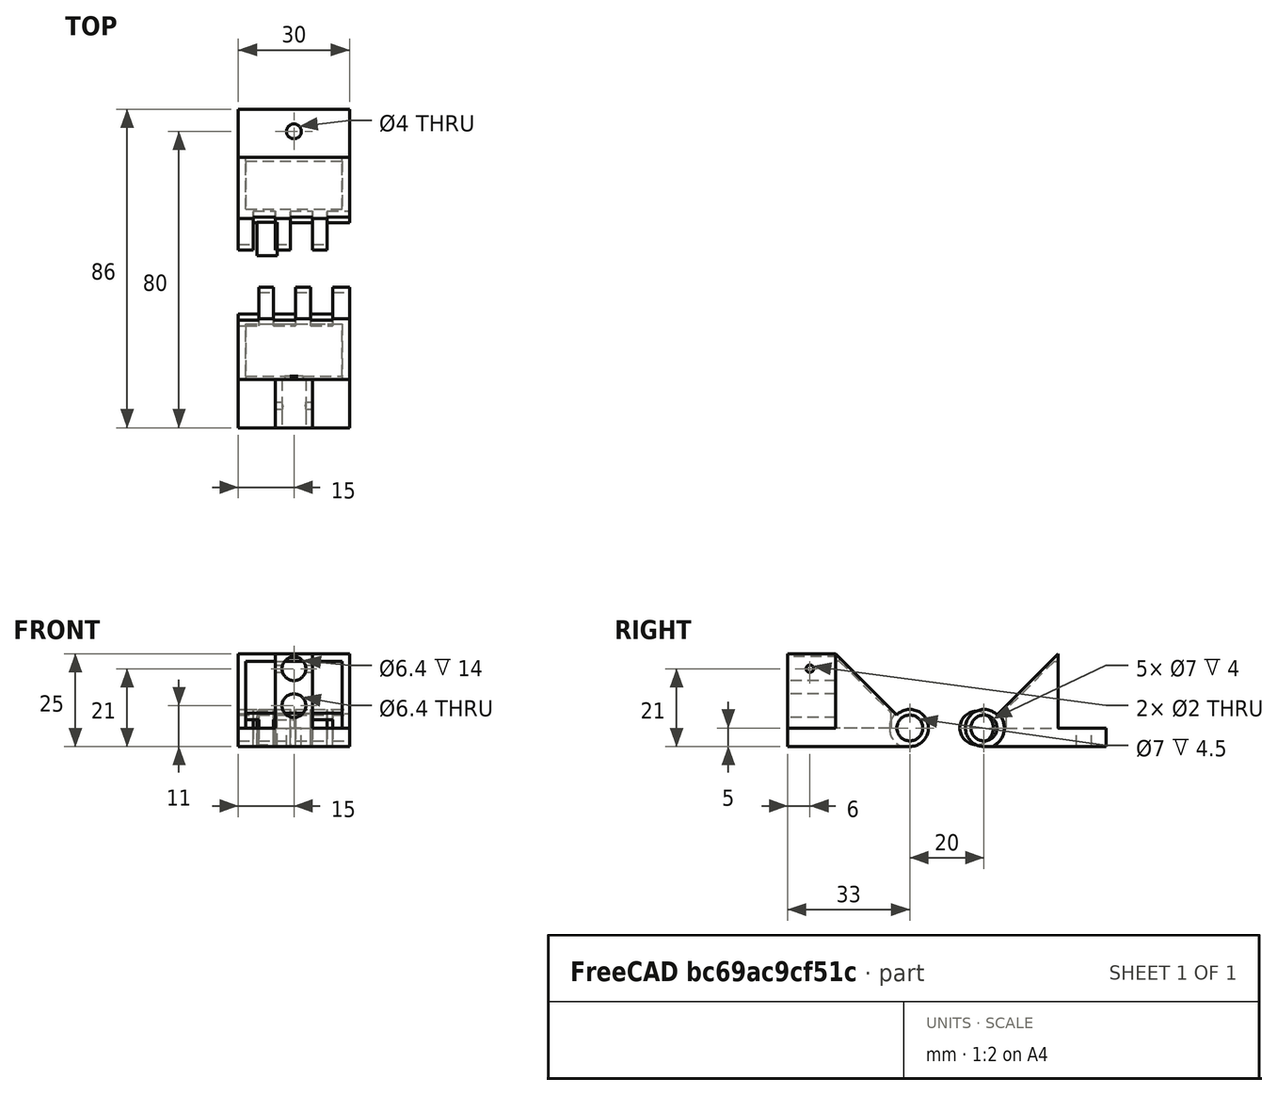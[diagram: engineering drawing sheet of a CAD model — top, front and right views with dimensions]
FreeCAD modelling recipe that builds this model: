
FCSTD DOCUMENT  (FreeCAD 0.16R6703 (Git))
Label: hinge_v3_0
License: CreativeCommons Attribution-ShareAlike
LicenseURL: http://creativecommons.org/licenses/by-sa/4.0/
objects: Part::Cut×12, Part::Box×11, Part::Cylinder×11, Part::MultiFuse×4, Part::FeaturePython×2, Part::Mirroring×1
note: 41 computed .brp shape members not serialized (recipe doc carries the construction recipe); baked Part::Feature solids carry a one-line shape summary decoded from their .brp

FEATURE [Part::Box] Box  label="Cube_out"
  Height = 20
  Length = 30
  Placement = pos=(-15,-5,-10) rot=(0,0,1;0rad)
  Width = 20
FEATURE [Part::Box] Box001  label="Cube_out_cut"
  Height = 15
  Length = 30
  Placement = pos=(-15,-5,-10) rot=(1,0,0;0.785398rad)
  Width = 34
FEATURE [Part::Cut] Cut
  Base = -> Box
  Tool = -> Box001
FEATURE [Part::Box] Box002  label="base"
  Height = 5
  Length = 30
  Placement = pos=(-15,-5,-15) rot=(0,0,1;0rad)
  Width = 33
FEATURE [Part::Cylinder] Cylinder  label="eje_out"
  Angle = 360
  Height = 30
  Placement = pos=(-15,-5,-10) rot=(0,1,0;1.5708rad)
  Radius = 5
FEATURE [Part::Box] Box003  label="Cube_int"
  Height = 18
  Length = 26
  Placement = pos=(-13,1,-10) rot=(0,0,1;0rad)
  Width = 20
FEATURE [Part::Box] Box004  label="Cube_int_cut"
  Height = 15
  Length = 30
  Placement = pos=(-15,-4,-10) rot=(1,0,0;0.785398rad)
  Width = 34
FEATURE [Part::Cut] Cut001
  Base = -> Box003
  Tool = -> Box004
FEATURE [Part::Cut] Cut002
  Base = -> Cut
  Tool = -> Cut001
FEATURE [Part::Cylinder] Cylinder001  label="eje_int"
  Angle = 360
  Height = 30
  Placement = pos=(-15,-5,-10) rot=(0,1,0;1.5708rad)
  Radius = 3.5
FEATURE [Part::MultiFuse] Fusion
  Shapes = -> [Cut002,Box002,Cylinder]
FEATURE [Part::Cut] Cut003
  Base = -> Fusion
  Tool = -> Cylinder001
FEATURE [Part::Box] Box005  label="Cube_out001"
  Height = 20
  Length = 30
  Placement = pos=(-15,-5,-10) rot=(0,0,1;0rad)
  Width = 20
FEATURE [Part::Box] Box006  label="Cube_out_cut001"
  Height = 15
  Length = 30
  Placement = pos=(-15,-5,-10) rot=(1,0,0;0.785398rad)
  Width = 34
FEATURE [Part::Cut] Cut004
  Base = -> Box005
  Tool = -> Box006
FEATURE [Part::Box] Box007  label="base001"
  Height = 5
  Length = 30
  Placement = pos=(-15,-5,-15) rot=(0,0,1;0rad)
  Width = 33
FEATURE [Part::Cylinder] Cylinder002  label="eje_out001"
  Angle = 360
  Height = 30
  Placement = pos=(-15,-5,-10) rot=(0,1,0;1.5708rad)
  Radius = 5
FEATURE [Part::Box] Box008  label="Cube_int001"
  Height = 18
  Length = 26
  Placement = pos=(-13,0,-10) rot=(0,0,1;0rad)
  Width = 20
FEATURE [Part::Box] Box009  label="Cube_int_cut001"
  Height = 15
  Length = 30
  Placement = pos=(-15,-4,-10) rot=(1,0,0;0.785398rad)
  Width = 34
FEATURE [Part::Cut] Cut005
  Base = -> Box008
  Tool = -> Box009
FEATURE [Part::Cut] Cut006
  Base = -> Cut004
  Tool = -> Cut005
FEATURE [Part::Cylinder] Cylinder003  label="eje_int001"
  Angle = 360
  Height = 30
  Placement = pos=(-15,-5,-10) rot=(0,1,0;1.5708rad)
  Radius = 3.5
FEATURE [Part::MultiFuse] Fusion001
  Shapes = -> [Cut006,Box007,Cylinder002]
FEATURE [Part::Cut] Cut007
  Base = -> Fusion001
  Tool = -> Cylinder003
FEATURE [Part::Mirroring] Part__Mirroring  label="Cut007 (Mirror #1)"
  Base = (0,-15,0)
  Normal = (0,1,0)
  Source = -> Cut007
FEATURE [Part::Cylinder] Cylinder004  label="eje_out002"
  Angle = 360
  Height = 6
  Placement = pos=(-11,-5,-10) rot=(0,1,0;1.5708rad)
  Radius = 5.5
FEATURE [Part::FeaturePython] Array  # Draft array (typed FeaturePython)
  Angle = 360
  ArrayType = 0
  Axis = (1,0,0)
  Base = -> Cylinder004
  Center = (0,0,0)
  Fuse = false
  IntervalAxis = (0,0,0)
  IntervalX = (10,0,0)
  IntervalY = (0,0,0)
  IntervalZ = (0,0,1)
  NumberPolar = 1
  NumberX = 4
  NumberY = 1
  NumberZ = 1
FEATURE [Part::Cylinder] Cylinder005  label="eje_out003"
  Angle = 360
  Height = 5.5
  Placement = pos=(-10,-7,-10) rot=(0,1,0;1.5708rad)
  Radius = 4.5
FEATURE [Part::Cut] Cut008
  Base = -> Cut003
  Tool = -> Array
FEATURE [Part::Cylinder] Cylinder006  label="eje_out004"
  Angle = 360
  Height = 6
  Placement = pos=(-15.5,-25,-10) rot=(0,1,0;1.5708rad)
  Radius = 5.5
FEATURE [Part::FeaturePython] Array001  # Draft array (typed FeaturePython)
  Angle = 360
  ArrayType = 0
  Axis = (0,0,1)
  Base = -> Cylinder006
  Center = (0,0,0)
  Fuse = false
  IntervalAxis = (0,0,0)
  IntervalX = (10,0,0)
  IntervalY = (0,1,0)
  IntervalZ = (0,0,0)
  NumberPolar = 1
  NumberX = 3
  NumberY = 1
  NumberZ = 1
FEATURE [Part::Cut] Cut009
  Base = -> Part__Mirroring
  Tool = -> Array001
FEATURE [Part::Cylinder] Cylinder007  label="tornillo"
  Angle = 360
  Height = 10
  Placement = pos=(0,22,-16) rot=(0,0,1;0rad)
  Radius = 2
FEATURE [Part::Cylinder] Cylinder008  label="Cylinder001"
  Angle = 360
  Height = 22
  Placement = pos=(0,-44,6) rot=(1,0,0;1.5708rad)
  Radius = 3.2
FEATURE [Part::Cut] Cut010
  Base = -> Cut008
  Tool = -> Cylinder007
FEATURE [Part::Box] Box010  label="Cube"
  Height = 21
  Length = 10
  Placement = pos=(-5,-58,-11) rot=(0,0,1;0rad)
  Width = 13
FEATURE [Part::Cylinder] Cylinder009  label="Cylinder002"
  Angle = 360
  Height = 22
  Placement = pos=(0,-44,-4) rot=(1,0,0;1.5708rad)
  Radius = 3.2
FEATURE [Part::Cylinder] Cylinder010  label="Cylinder003"
  Angle = 360
  Height = 22
  Placement = pos=(-12,-52,6) rot=(0,1,0;1.5708rad)
  Radius = 1
FEATURE [Part::MultiFuse] Fusion002
  Shapes = -> [Cylinder008,Cylinder009,Cylinder010]
FEATURE [Part::MultiFuse] Fusion003
  Shapes = -> [Cut009,Box010]
FEATURE [Part::Cut] Cut011
  Base = -> Fusion003
  Tool = -> Fusion002
